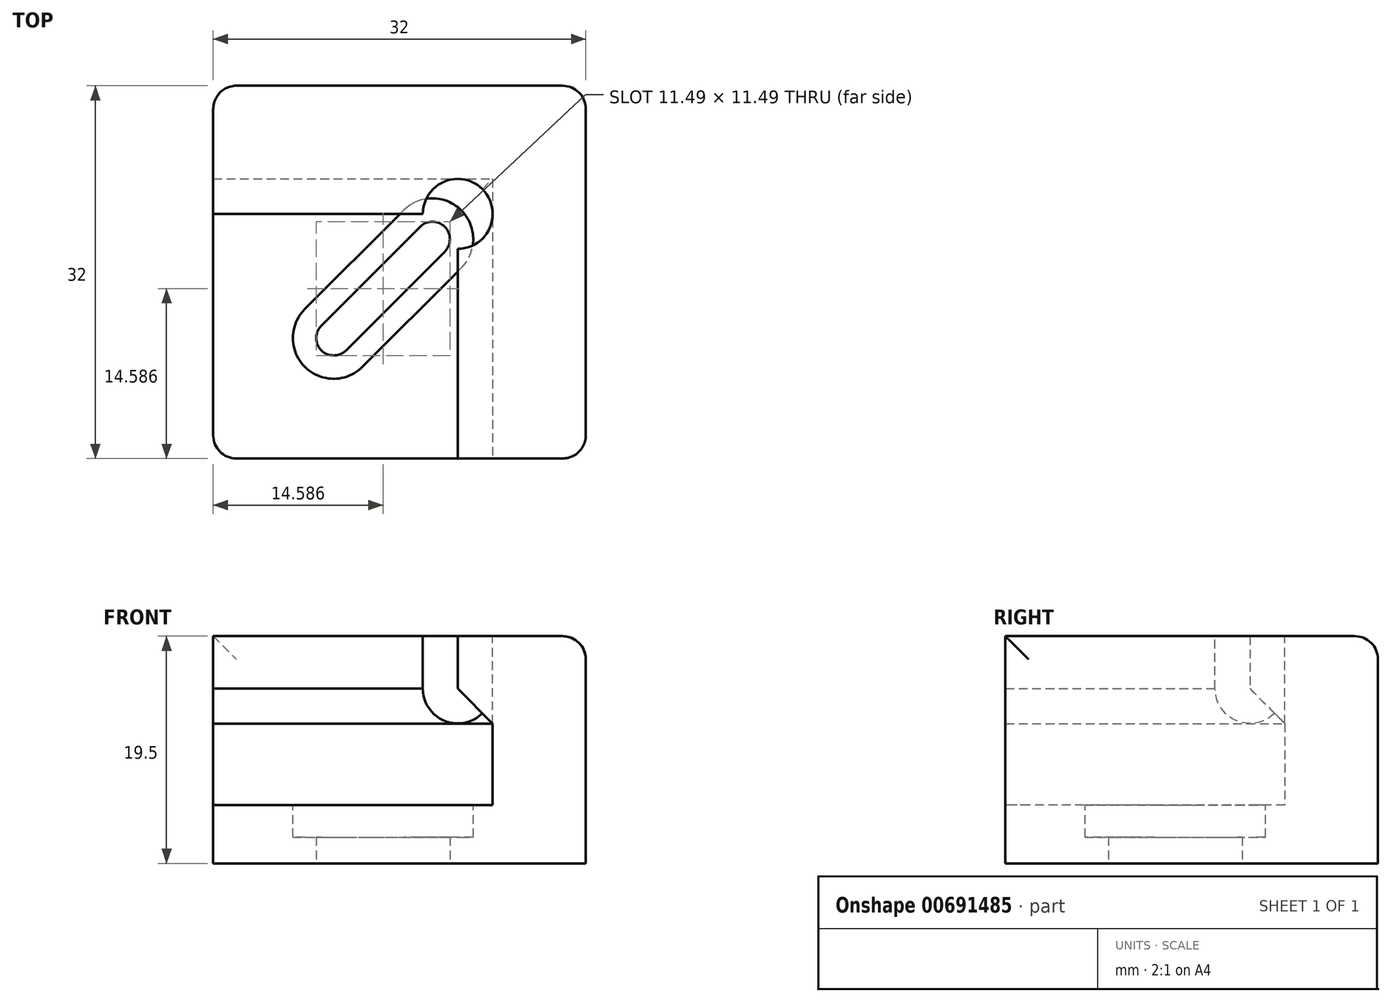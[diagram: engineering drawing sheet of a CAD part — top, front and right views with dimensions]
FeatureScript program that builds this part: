
annotation { "Feature Type Name" : "Feature", "Feature Type Description" : "" }
export const myFeature = defineFeature(function(context is Context, id is Id, definition is map)
    precondition{}
    {
        {
            var Q0;
            Q0=qCreatedBy(makeId("Top.planeOp"),FACE);
            var sketch = newSketch(context, id + "F0", { "sketchPlane" : qUnion([Q0])});
            skLineSegment(sketch, "E0.bottom", {"start": v(16, 16) * mm, "end": v(-16, 16) * mm});
            skLineSegment(sketch, "E0.top", {"start": v(16, -16) * mm, "end": v(-16, -16) * mm});
            skLineSegment(sketch, "E0.left", {"start": v(16, 16) * mm, "end": v(16, -16) * mm});
            skLineSegment(sketch, "E0.right", {"start": v(-16, 16) * mm, "end": v(-16, -16) * mm});
            skPoint(sketch, "E0.middle", {"position": v(0, 0) * mm});
            skLineSegment(sketch, "E1", {"start": v(16, 16) * mm, "end": v(-16, -16) * mm, "construction": true});
            skArc(sketch, "E2", {"start": v(-6.72, -4.6) * mm, "mid": v(-6.72, -6.72) * mm, "end": v(-4.6, -6.72) * mm});
            skArc(sketch, "E3", {"start": v(3.89, 1.77) * mm, "mid": v(3.89, 3.89) * mm, "end": v(1.77, 3.89) * mm});
            skLineSegment(sketch, "E4", {"start": v(-6.72, -4.6) * mm, "end": v(1.77, 3.89) * mm});
            skLineSegment(sketch, "E5", {"start": v(-4.6, -6.72) * mm, "end": v(3.89, 1.77) * mm});
            skSolve(sketch);
        }
        {
            var Q0;
            Q0 = qSketchRegion(id + "F0", true);
            extrude(context, id + "F1", {"entities" : qUnion([Q0]), "depth" : 5 * mm, "offsetDistance" : 25 * mm});
        }
        {
            var Q0;
            Q0=makeQuery(id+"F1.opExtrude","CAP_FACE",FACE,{"disambiguationData":[OSD([sQuery(id+"F0.wireOp",EDGE,"E0.bottom"),sQuery(id+"F0.wireOp",EDGE,"E0.top"),sQuery(id+"F0.wireOp",EDGE,"E0.left"),sQuery(id+"F0.wireOp",EDGE,"E0.right"),sQuery(id+"F0.wireOp",EDGE,"E2"),sQuery(id+"F0.wireOp",EDGE,"P4IrOFUm-jsfK-PEYB-a1kb-UOc8P7vN9Hze"),sQuery(id+"F0.wireOp",EDGE,"Z9PYAiSD-VbMn-QlA7-J8ej-kAA6el6lO6gk"),sQuery(id+"F0.wireOp",EDGE,"9x8ULy2D-pp7w-t5rr-2Edc-2ipPcrbERmze")])],"isStart":false});
            var sketch = newSketch(context, id + "F2", { "sketchPlane" : qUnion([Q0])});
            skLineSegment(sketch, "E6", {"start": v(-16, 8) * mm, "end": v(8, 8) * mm});
            skLineSegment(sketch, "E7", {"start": v(8, 8) * mm, "end": v(8, -16) * mm});
            skArc(sketch, "E8", {"start": v(-8.13, -3.18) * mm, "mid": v(-8.13, -8.13) * mm, "end": v(-3.18, -8.13) * mm});
            skArc(sketch, "E9", {"start": v(5.3, 0.35) * mm, "mid": v(5.3, 5.3) * mm, "end": v(0.35, 5.3) * mm});
            skLineSegment(sketch, "E10", {"start": v(-8.13, -3.18) * mm, "end": v(0.35, 5.3) * mm});
            skLineSegment(sketch, "E11", {"start": v(-3.18, -8.13) * mm, "end": v(5.3, 0.35) * mm});
            skSolve(sketch);
        }
        {
            var Q0;
            {var subQ4=sQuery(id+"F2.wireOp",EDGE,"E6");Q0=makeQuery(id+"F2.imprint","IMPRINT",FACE,{"disambiguationData":[TD([[makeQuery(id+"F2.imprint","IMPRINT",EDGE,{"derivedFrom":subQ4}),1.0]])]});}
            extrude(context, id + "F3", {"entities" : qUnion([Q0]), "operationType" : NewBodyOperationType.ADD, "depth" : 14.5 * mm, "offsetDistance" : 25 * mm});
        }
        {
            var Q0;
            Q0=makeQuery(id+"F2.imprint","IMPRINT",FACE,{"disambiguationData":[TD([[makeQuery(id+"F2.imprint","IMPRINT",EDGE,{"derivedFrom":sQuery(id+"F2.wireOp",EDGE,"E8")}),1.0]])]});
            extrude(context, id + "F4", {"entities" : qUnion([Q0]), "operationType" : NewBodyOperationType.REMOVE, "oppositeDirection" : true, "depth" : 2.75 * mm, "offsetDistance" : 25 * mm});
        }
        {
            var Q0;
            {var subQ0=sQuery(id+"F0.wireOp",EDGE,"E0.top");Q0=makeQuery(id+"F3.boolean.opBoolean","MERGE",FACE,{"derivedFrom":[makeQuery(id+"F1.opExtrude","SWEPT_FACE",FACE,{"disambiguationData":[OSD([subQ0])]}),makeQuery(id+"F3.opExtrude","SWEPT_FACE",FACE,{"disambiguationData":[OSD([subQ0])]})]});}
            var sketch = newSketch(context, id + "F5", { "sketchPlane" : qUnion([Q0])});
            skLineSegment(sketch, "E12", {"start": v(8, 19.5) * mm, "end": v(5, 19.5) * mm});
            skLineSegment(sketch, "E13", {"start": v(5, 19.5) * mm, "end": v(5, 15) * mm});
            skLineSegment(sketch, "E14", {"start": v(5, 15) * mm, "end": v(8, 12) * mm});
            skSolve(sketch);
        }
        {
            var Q0;
            {var subQ0=sQuery(id+"F5.wireOp",EDGE,"E12");Q0=makeQuery(id+"F5.imprint","IMPRINT",FACE,{"disambiguationData":[TD([[makeQuery(id+"F5.imprint","IMPRINT",EDGE,{"derivedFrom":subQ0}),1.0]])]});}
            var Q1;
            Q1=makeQuery(id+"F3.opExtrude","CAP_EDGE",EDGE,{"disambiguationData":[OSD([sQuery(id+"F2.wireOp",EDGE,"E6")])],"isStart":false});
            var Q2;
            Q2=makeQuery(id+"F3.opExtrude","CAP_EDGE",EDGE,{"disambiguationData":[OSD([sQuery(id+"F2.wireOp",EDGE,"E7")])],"isStart":false});
            sweep(context, id + "F6", {"operationType" : NewBodyOperationType.ADD, "profiles" : qUnion([Q0]), "path" : qUnion([Q1, Q2])});
        }
        {
            var Q0;
            {var subQ0=sQuery(id+"F2.wireOp",EDGE,"E7");Q0=makeQuery(id+"F6.boolean.opBoolean","MERGE",FACE,{"derivedFrom":[makeQuery(id+"F3.opExtrude","CAP_FACE",FACE,{"disambiguationData":[OSD([sQuery(id+"F0.wireOp",EDGE,"E0.bottom"),sQuery(id+"F0.wireOp",EDGE,"E0.top"),sQuery(id+"F0.wireOp",EDGE,"E0.left"),sQuery(id+"F0.wireOp",EDGE,"E0.right"),sQuery(id+"F2.wireOp",EDGE,"E6"),subQ0])],"isStart":false}),makeQuery(id+"F6.opSweep","SWEPT_FACE",FACE,{"disambiguationData":[OSD([subQ0,sQuery(id+"F5.wireOp",EDGE,"E12")])]})]});}
            var sketch = newSketch(context, id + "F7", { "sketchPlane" : qUnion([Q0])});
            skCircle(sketch, "E15", {"center": v(5, 5) * mm, "radius": 3 * mm});
            skSolve(sketch);
        }
        {
            var Q0;
            Q0 = qSketchRegion(id + "F7", true);
            extrude(context, id + "F8", {"entities" : qUnion([Q0]), "operationType" : NewBodyOperationType.REMOVE, "oppositeDirection" : true, "depth" : 14 * mm, "offsetDistance" : 25 * mm});
        }
        {
            var Q0;
            {var subQ0=sQuery(id+"F0.wireOp",EDGE,"E0.left");var subQ1=sQuery(id+"F0.wireOp",EDGE,"E0.top");Q0=makeQuery(id+"F3.boolean.opBoolean","MERGE",EDGE,{"derivedFrom":[makeQuery(id+"F1.opExtrude","SWEPT_EDGE",EDGE,{"disambiguationData":[OSD([subQ1,subQ0])]}),makeQuery(id+"F3.opExtrude","SWEPT_EDGE",EDGE,{"disambiguationData":[OSD([subQ1,subQ0])]})]});}
            var Q1;
            {var subQ0=sQuery(id+"F0.wireOp",EDGE,"E0.left");var subQ1=sQuery(id+"F0.wireOp",EDGE,"E0.bottom");Q1=makeQuery(id+"F3.boolean.opBoolean","MERGE",EDGE,{"derivedFrom":[makeQuery(id+"F1.opExtrude","SWEPT_EDGE",EDGE,{"disambiguationData":[OSD([subQ1,subQ0])]}),makeQuery(id+"F3.opExtrude","SWEPT_EDGE",EDGE,{"disambiguationData":[OSD([subQ1,subQ0])]})]});}
            var Q2;
            {var subQ0=sQuery(id+"F0.wireOp",EDGE,"E0.right");var subQ1=sQuery(id+"F0.wireOp",EDGE,"E0.bottom");Q2=makeQuery(id+"F3.boolean.opBoolean","MERGE",EDGE,{"derivedFrom":[makeQuery(id+"F1.opExtrude","SWEPT_EDGE",EDGE,{"disambiguationData":[OSD([subQ1,subQ0])]}),makeQuery(id+"F3.opExtrude","SWEPT_EDGE",EDGE,{"disambiguationData":[OSD([subQ1,subQ0])]})]});}
            var Q3;
            Q3=makeQuery(id+"F3.opExtrude","CAP_EDGE",EDGE,{"disambiguationData":[OSD([sQuery(id+"F0.wireOp",EDGE,"E0.bottom")])],"isStart":false});
            var Q4;
            Q4=makeQuery(id+"F3.opExtrude","CAP_EDGE",EDGE,{"disambiguationData":[OSD([sQuery(id+"F0.wireOp",EDGE,"E0.left")])],"isStart":false});
            var Q5;
            Q5=makeQuery(id+"F1.opExtrude","SWEPT_EDGE",EDGE,{"disambiguationData":[OSD([sQuery(id+"F0.wireOp",EDGE,"E0.top"),sQuery(id+"F0.wireOp",EDGE,"E0.right")])]});
            fillet(context, id + "F9", {"entities" : qUnion([Q0, Q1, Q2, Q3, Q4, Q5]), "radius" : 2 * mm, "tangentPropagation" : true, "allowEdgeOverflow" : false});
        }
    });
